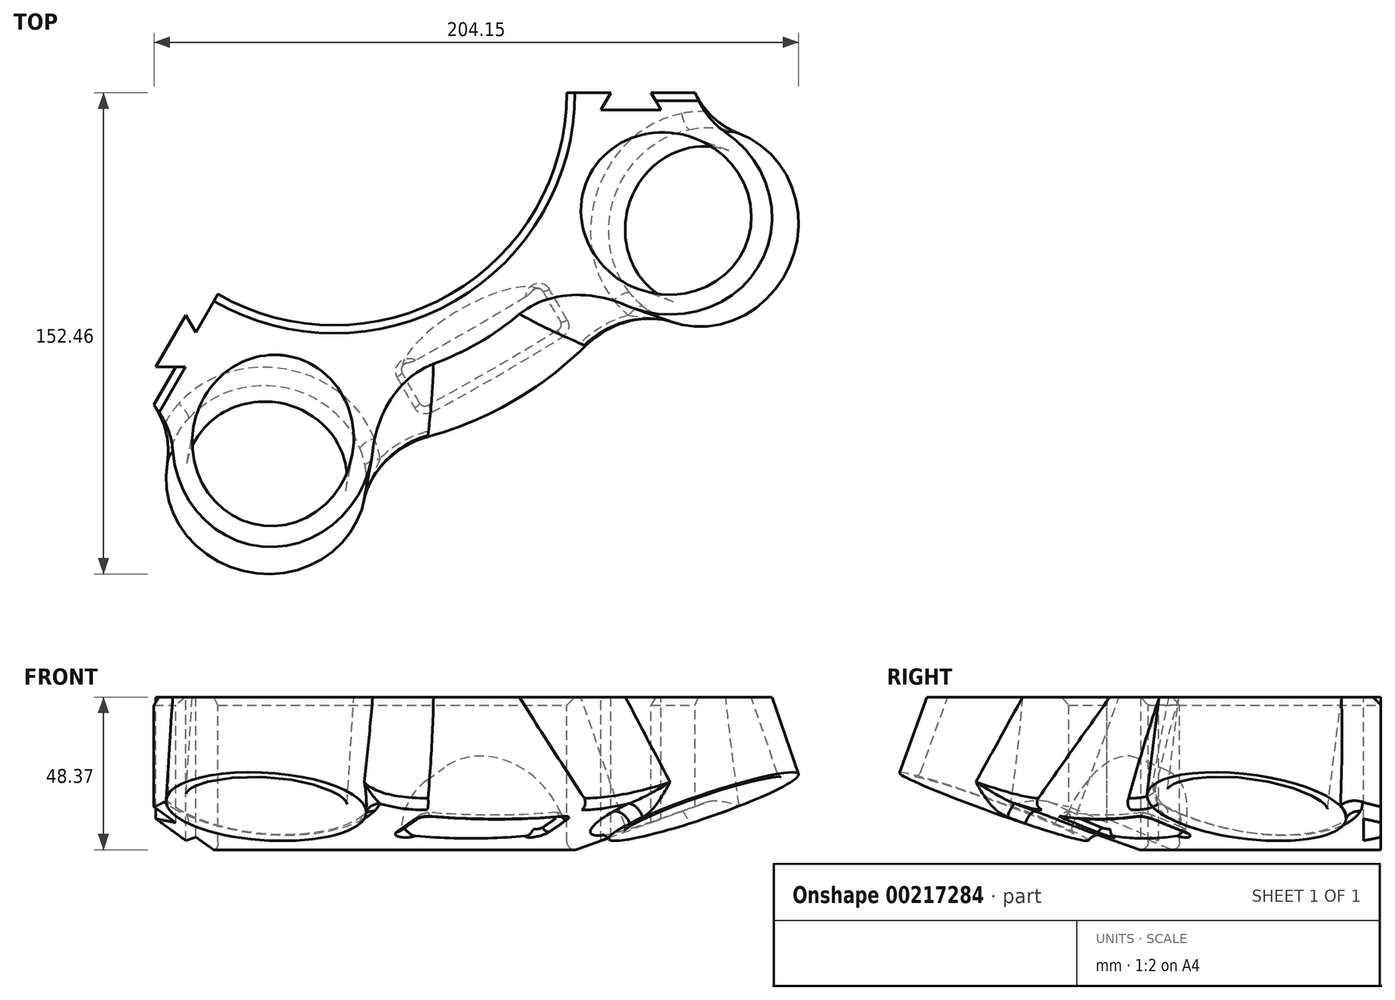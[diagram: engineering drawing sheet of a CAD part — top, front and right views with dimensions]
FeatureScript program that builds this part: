
annotation { "Feature Type Name" : "Feature", "Feature Type Description" : "" }
export const myFeature = defineFeature(function(context is Context, id is Id, definition is map)
    precondition{}
    {
        {
            var Q0;
            Q0=qCreatedBy(makeId("Top.planeOp"),FACE);
            var sketch = newSketch(context, id + "F0", { "sketchPlane" : qUnion([Q0])});
            skArc(sketch, "E0", {"start": v(36.2, 62.7) * mm, "mid": v(-36.2, 62.7) * mm, "end": v(-72.39, 0) * mm});
            skArc(sketch, "E1", {"start": v(55.44, 96.02) * mm, "mid": v(43.6, 101.94) * mm, "end": v(31.13, 106.41) * mm});
            skLineSegment(sketch, "E2", {"start": v(-72.4, 0) * mm, "end": v(-110.87, 0) * mm});
            skLineSegment(sketch, "E3", {"start": v(36.2, 62.7) * mm, "end": v(55.44, 96.02) * mm});
            skLineSegment(sketch, "E4", {"start": v(-22.63, 115.53) * mm, "end": v(0, 0) * mm, "construction": true});
            skLineSegment(sketch, "E5", {"start": v(-90.19, 75.67) * mm, "end": v(0, 0) * mm, "construction": true});
            skPoint(sketch, "E6.visualSharp", {"position": v(-104.04, 38.3) * mm});
            skPoint(sketch, "E7.visualSharp", {"position": v(-57.88, 98.1) * mm});
            skPoint(sketch, "E8.visualSharp", {"position": v(16.78, 109.6) * mm});
            skArc(sketch, "E9.converted", {"start": v(55.44, 96.02) * mm, "mid": v(-55.44, 96.02) * mm, "end": v(-110.87, 0) * mm});
            skSolve(sketch);
        }
        {
            var Q0;
            Q0=qCreatedBy(makeId("Front.planeOp"),FACE);
            var Q1;
            Q1=sQuery(id+"F0.wireOp",EDGE,"E5");
            cPlane(context, id + "F1", {"entities" : qUnion([Q0, Q1]), "cplaneType" : CPlaneType.LINE_ANGLE, "offset" : 25.4 * mm, "angle" : 0 * degree, "width" : 152.4 * mm, "height" : 152.4 * mm});
        }
        {
            var Q0;
            Q0=qCreatedBy(id+"F1.planeOp",FACE);
            var sketch = newSketch(context, id + "F2", { "sketchPlane" : qUnion([Q0])});
            skLineSegment(sketch, "E10", {"start": v(91.59, 0) * mm, "end": v(119.1, 10.02) * mm, "construction": true});
            skSolve(sketch);
        }
        {
            var Q0;
            Q0=qCreatedBy(id+"F1.planeOp",FACE);
            var Q1;
            Q1=sQuery(id+"F0.wireOp",EDGE,"E4");
            cPlane(context, id + "F3", {"entities" : qUnion([Q0, Q1]), "cplaneType" : CPlaneType.LINE_ANGLE, "offset" : 25.4 * mm, "angle" : 0 * degree, "width" : 152.4 * mm, "height" : 152.4 * mm});
        }
        {
            var Q0;
            Q0=qCreatedBy(id+"F3.planeOp",FACE);
            var sketch = newSketch(context, id + "F4", { "sketchPlane" : qUnion([Q0])});
            skLineSegment(sketch, "E11", {"start": v(-91.91, 0) * mm, "end": v(-139.27, 17.24) * mm, "construction": true});
            skSolve(sketch);
        }
        {
            var Q0;
            Q0=qCreatedBy(id+"F1.planeOp",FACE);
            var sketch = newSketch(context, id + "F5", { "sketchPlane" : qUnion([Q0])});
            skLineSegment(sketch, "E12", {"start": v(0, 0) * mm, "end": v(124.46, 0) * mm, "construction": true});
            skLineSegment(sketch, "E13", {"start": v(0, 53.66) * mm, "end": v(0, 0) * mm, "construction": true});
            skLineSegment(sketch, "E14", {"start": v(124.46, 0) * mm, "end": v(106, 50.72) * mm, "construction": true});
            skLineSegment(sketch, "E15", {"start": v(148.36, 8.7) * mm, "end": v(154.3, 10.86) * mm});
            skLineSegment(sketch, "E16", {"start": v(154.3, 10.86) * mm, "end": v(134.75, 64.56) * mm});
            skLineSegment(sketch, "E17", {"start": v(134.75, 64.56) * mm, "end": v(129.03, 61.8) * mm});
            skLineSegment(sketch, "E18", {"start": v(148.36, 8.7) * mm, "end": v(129.03, 61.8) * mm});
            skSolve(sketch);
        }
        {
            var Q0;
            Q0=qSketchRegion(id+"F5",true);
            var Q1;
            Q1=sQuery(id+"F5.wireOp",EDGE,"E14");
            revolve(context, id + "F6", {"entities" : qUnion([Q0]), "axis" : qUnion([Q1]), "revolveType" : RevolveType.FULL});
        }
        {
            var Q0;
            Q0=makeQuery(id+"F6.opRevolve","SWEPT_BODY",BODY,{"disambiguationData":[OSD([sQuery(id+"F5.wireOp",EDGE,"E15"),sQuery(id+"F5.wireOp",EDGE,"E16"),sQuery(id+"F5.wireOp",EDGE,"E17"),sQuery(id+"F5.wireOp",EDGE,"E18")])]});
            var Q1;
            Q1=sQuery(id+"F5.wireOp",EDGE,"E13");
            circularPattern(context, id + "F7", {"entities" : qUnion([Q0]), "axis" : qUnion([Q1]), "angle" : 40 * degree, "instanceCount" : 2});
        }
        {
            var Q0;
            Q0=qCreatedBy(id+"F1.planeOp",FACE);
            var sketch = newSketch(context, id + "F8", { "sketchPlane" : qUnion([Q0])});
            skLineSegment(sketch, "E19", {"start": v(73.66, 34.68) * mm, "end": v(73.66, -14.78) * mm});
            skLineSegment(sketch, "E20", {"start": v(73.66, -14.78) * mm, "end": v(73.66, 34.68) * mm});
            skLineSegment(sketch, "E21", {"start": v(73.66, 34.68) * mm, "end": v(91.44, 34.68) * mm});
            skLineSegment(sketch, "E22", {"start": v(114.27, 0) * mm, "end": v(73.66, -14.78) * mm});
            skLineSegment(sketch, "E23", {"start": v(91.44, 34.68) * mm, "end": v(114.27, 0) * mm});
            skSolve(sketch);
        }
        {
            var Q0;
            Q0=qSketchRegion(id+"F8",true);
            var Q1;
            Q1=sQuery(id+"F5.wireOp",EDGE,"E13");
            revolve(context, id + "F9", {"entities" : qUnion([Q0]), "axis" : qUnion([Q1]), "revolveType" : RevolveType.TWO_DIRECTIONS, "angle" : 80 * degree, "angleBack" : 320 * degree});
        }
        {
            var Q0;
            Q0=makeQuery(id+"F6.opRevolve","SWEPT_FACE",FACE,{"disambiguationData":[OSD([sQuery(id+"F5.wireOp",EDGE,"E15")])]});
            var sketch = newSketch(context, id + "F10", { "sketchPlane" : qUnion([Q0])});
            skCircle(sketch, "E24", {"center": v(-87.24, -77.9) * mm, "radius": 25.53 * mm});
            skSolve(sketch);
        }
        {
            var Q0;
            Q0=qSketchRegion(id+"F10",true);
            extrude(context, id + "F11", {"entities" : qUnion([Q0]), "operationType" : NewBodyOperationType.REMOVE, "endBound" : BoundingType.THROUGH_ALL, "depth" : 25.4 * mm, "hasSecondDirection" : true, "secondDirectionBound" : SecondDirectionBoundingType.THROUGH_ALL, "secondDirectionOppositeDirection" : true, "secondDirectionDepth" : 25.4 * mm});
        }
        {
            var Q0;
            Q0=makeQuery(id+"F7.opPattern","COPY",FACE,{"derivedFrom":makeQuery(id+"F6.opRevolve","SWEPT_FACE",FACE,{"disambiguationData":[OSD([sQuery(id+"F5.wireOp",EDGE,"E15")])]}),"instanceName":"1"});
            var sketch = newSketch(context, id + "F12", { "sketchPlane" : qUnion([Q0])});
            skCircle(sketch, "E25", {"center": v(-19.12, -115.38) * mm, "radius": 25.53 * mm});
            skSolve(sketch);
        }
        {
            var Q0;
            Q0=qSketchRegion(id+"F12",true);
            extrude(context, id + "F13", {"entities" : qUnion([Q0]), "operationType" : NewBodyOperationType.REMOVE, "endBound" : BoundingType.THROUGH_ALL, "depth" : 25.4 * mm, "hasSecondDirection" : true, "secondDirectionBound" : SecondDirectionBoundingType.THROUGH_ALL, "secondDirectionOppositeDirection" : true, "secondDirectionDepth" : 25.4 * mm});
        }
        {
            var Q0;
            Q0=makeQuery(id+"F9.opRevolve","CAP_FACE",FACE,{"disambiguationData":[OSD([sQuery(id+"F8.wireOp",EDGE,"E19"),sQuery(id+"F8.wireOp",EDGE,"E20"),sQuery(id+"F8.wireOp",EDGE,"E21"),sQuery(id+"F8.wireOp",EDGE,"E22"),sQuery(id+"F8.wireOp",EDGE,"E23")])],"isStart":true});
            var sketch = newSketch(context, id + "F14", { "sketchPlane" : qUnion([Q0])});
            skLineSegment(sketch, "E26", {"start": v(-73.66, 34.68) * mm, "end": v(-150.81, 34.68) * mm});
            skLineSegment(sketch, "E27", {"start": v(-150.81, 69.54) * mm, "end": v(-73.66, 69.54) * mm});
            skLineSegment(sketch, "E28", {"start": v(-150.81, 69.54) * mm, "end": v(-150.81, 34.68) * mm});
            skLineSegment(sketch, "E29", {"start": v(-73.66, 69.54) * mm, "end": v(-73.66, 34.68) * mm});
            skSolve(sketch);
        }
        {
            var Q0;
            Q0=qSketchRegion(id+"F14",true);
            var Q1;
            Q1=sQuery(id+"F5.wireOp",EDGE,"E13");
            revolve(context, id + "F15", {"operationType" : NewBodyOperationType.REMOVE, "entities" : qUnion([Q0]), "axis" : qUnion([Q1]), "revolveType" : RevolveType.ONE_DIRECTION, "angle" : 120 * degree});
        }
        {
            var Q0;
            Q0=makeQuery(id+"F6.opRevolve","SWEPT_BODY",BODY,{"disambiguationData":[OSD([sQuery(id+"F5.wireOp",EDGE,"E15"),sQuery(id+"F5.wireOp",EDGE,"E16"),sQuery(id+"F5.wireOp",EDGE,"E17"),sQuery(id+"F5.wireOp",EDGE,"E18")])]});
            var Q1;
            Q1=makeQuery(id+"F7.opPattern","COPY",BODY,{"derivedFrom":makeQuery(id+"F6.opRevolve","SWEPT_BODY",BODY,{"disambiguationData":[OSD([sQuery(id+"F5.wireOp",EDGE,"E15"),sQuery(id+"F5.wireOp",EDGE,"E16"),sQuery(id+"F5.wireOp",EDGE,"E17"),sQuery(id+"F5.wireOp",EDGE,"E18")])]}),"instanceName":"1"});
            var Q2;
            Q2=makeQuery(id+"F9.opRevolve","SWEPT_BODY",BODY,{"disambiguationData":[OSD([sQuery(id+"F8.wireOp",EDGE,"E19"),sQuery(id+"F8.wireOp",EDGE,"E20"),sQuery(id+"F8.wireOp",EDGE,"E21"),sQuery(id+"F8.wireOp",EDGE,"E22"),sQuery(id+"F8.wireOp",EDGE,"E23")])]});
            var Q3;
            Q3=sQuery(id+"F5.wireOp",EDGE,"E13");
            circularPattern(context, id + "F16", {"entities" : qUnion([Q0, Q1, Q2]), "axis" : qUnion([Q3]), "angle" : 120 * degree, "instanceCount" : 3});
        }
        {
            var Q0;
            Q0=qCreatedBy(makeId("Front.planeOp"),FACE);
            var sketch = newSketch(context, id + "F17", { "sketchPlane" : qUnion([Q0])});
            skLineSegment(sketch, "E30", {"start": v(-105.19, -47.93) * mm, "end": v(-151.02, -47.93) * mm, "construction": true});
            skLineSegment(sketch, "E31", {"start": v(-102.98, -8.48) * mm, "end": v(-100.37, -1.32) * mm});
            skLineSegment(sketch, "E32", {"start": v(-102.98, -8.48) * mm, "end": v(-129.23, 1.07) * mm});
            skLineSegment(sketch, "E33", {"start": v(-129.23, 1.07) * mm, "end": v(-126.63, 8.23) * mm});
            skLineSegment(sketch, "E34", {"start": v(-126.63, 8.23) * mm, "end": v(-100.37, -1.32) * mm});
            skLineSegment(sketch, "E35", {"start": v(-135.33, -8.25) * mm, "end": v(-127.68, 12.78) * mm, "construction": true});
            skSolve(sketch);
        }
        {
            var Q0;
            Q0=makeQuery(id+"FokKAQGzDr6NISq_2.opRevolve","SWEPT_BODY",BODY,{"disambiguationData":[OSD([sQuery(id+"F17.wireOp",EDGE,"E31"),sQuery(id+"F17.wireOp",EDGE,"E32"),sQuery(id+"F17.wireOp",EDGE,"E33"),sQuery(id+"F17.wireOp",EDGE,"E34")])]});
            var Q1;
            Q1=makeQuery(id+"F9.opRevolve","SWEPT_BODY",BODY,{"disambiguationData":[OSD([sQuery(id+"F8.wireOp",EDGE,"E19"),sQuery(id+"F8.wireOp",EDGE,"E20"),sQuery(id+"F8.wireOp",EDGE,"E21"),sQuery(id+"F8.wireOp",EDGE,"E22"),sQuery(id+"F8.wireOp",EDGE,"E23")])]});
            var Q2;
            Q2=sQuery(id+"F5.wireOp",EDGE,"E13");
            circularPattern(context, id + "F18", {"entities" : qUnion([Q0, Q1]), "axis" : qUnion([Q2]), "angle" : 120 * degree, "instanceCount" : 3});
        }
        {
            var Q0;
            {var subQ0=sQuery(id+"F8.wireOp",EDGE,"E22");var subQ2=sQuery(id+"F8.wireOp",EDGE,"E23");var subQ4=sQuery(id+"F8.wireOp",EDGE,"E21");var subQ5=makeQuery(id+"F11.opExtrude","SWEPT_FACE",FACE,{"disambiguationData":[OSD([sQuery(id+"F10.wireOp",EDGE,"E24")])]});Q0=makeQuery(id+"F16.opPattern","COPY",EDGE,{"derivedFrom":makeQuery(id+"F13.boolean.opBoolean","SPLIT",EDGE,{"disambiguationData":[TD([makeQuery(id+"F11.boolean.opBoolean","COPY",FACE,{"disambiguationData":[TD([makeQuery(id+"F9.opRevolve","SWEPT_FACE",FACE,{"disambiguationData":[OSD([subQ4])]})])],"derivedFrom":subQ5})])],"derivedFrom":makeQuery(id+"F11.boolean.opBoolean","SPLIT",EDGE,{"disambiguationData":[TD([makeQuery(id+"F9.opRevolve","CAP_FACE",FACE,{"disambiguationData":[OSD([sQuery(id+"F8.wireOp",EDGE,"E19"),sQuery(id+"F8.wireOp",EDGE,"E20"),subQ4,subQ0,subQ2])],"isStart":false})])],"derivedFrom":makeQuery(id+"F9.opRevolve","SWEPT_EDGE",EDGE,{"disambiguationData":[OSD([subQ0,subQ2])]})})}),"instanceName":"1"});}
            fillet(context, id + "F19", {"entities" : qUnion([Q0]), "radius" : 5.08 * mm, "tangentPropagation" : true, "allowEdgeOverflow" : false});
        }
        {
            var Q0;
            Q0=makeQuery(id+"F18.opPattern","COPY",BODY,{"derivedFrom":makeQuery(id+"FokKAQGzDr6NISq_2.opRevolve","SWEPT_BODY",BODY,{"disambiguationData":[OSD([sQuery(id+"F17.wireOp",EDGE,"E31"),sQuery(id+"F17.wireOp",EDGE,"E32"),sQuery(id+"F17.wireOp",EDGE,"E33"),sQuery(id+"F17.wireOp",EDGE,"E34")])]}),"instanceName":"1"});
            var Q1;
            Q1=makeQuery(id+"F6.opRevolve","SWEPT_BODY",BODY,{"disambiguationData":[OSD([sQuery(id+"F5.wireOp",EDGE,"E15"),sQuery(id+"F5.wireOp",EDGE,"E16"),sQuery(id+"F5.wireOp",EDGE,"E17"),sQuery(id+"F5.wireOp",EDGE,"E18")])]});
            var Q2;
            Q2=makeQuery(id+"F16.opPattern","COPY",BODY,{"derivedFrom":makeQuery(id+"F9.opRevolve","SWEPT_BODY",BODY,{"disambiguationData":[OSD([sQuery(id+"F8.wireOp",EDGE,"E19"),sQuery(id+"F8.wireOp",EDGE,"E20"),sQuery(id+"F8.wireOp",EDGE,"E21"),sQuery(id+"F8.wireOp",EDGE,"E22"),sQuery(id+"F8.wireOp",EDGE,"E23")])]}),"instanceName":"1"});
            var Q3;
            Q3=makeQuery(id+"F18.opPattern","COPY",BODY,{"derivedFrom":makeQuery(id+"F9.opRevolve","SWEPT_BODY",BODY,{"disambiguationData":[OSD([sQuery(id+"F8.wireOp",EDGE,"E19"),sQuery(id+"F8.wireOp",EDGE,"E20"),sQuery(id+"F8.wireOp",EDGE,"E21"),sQuery(id+"F8.wireOp",EDGE,"E22"),sQuery(id+"F8.wireOp",EDGE,"E23")])]}),"instanceName":"1"});
            var Q4;
            Q4=makeQuery(id+"F18.opPattern","COPY",BODY,{"derivedFrom":makeQuery(id+"F9.opRevolve","SWEPT_BODY",BODY,{"disambiguationData":[OSD([sQuery(id+"F8.wireOp",EDGE,"E19"),sQuery(id+"F8.wireOp",EDGE,"E20"),sQuery(id+"F8.wireOp",EDGE,"E21"),sQuery(id+"F8.wireOp",EDGE,"E22"),sQuery(id+"F8.wireOp",EDGE,"E23")])]}),"instanceName":"2"});
            var Q5;
            Q5=makeQuery(id+"F7.opPattern","COPY",BODY,{"derivedFrom":makeQuery(id+"F6.opRevolve","SWEPT_BODY",BODY,{"disambiguationData":[OSD([sQuery(id+"F5.wireOp",EDGE,"E15"),sQuery(id+"F5.wireOp",EDGE,"E16"),sQuery(id+"F5.wireOp",EDGE,"E17"),sQuery(id+"F5.wireOp",EDGE,"E18")])]}),"instanceName":"1"});
            var Q6;
            Q6=makeQuery(id+"F16.opPattern","COPY",BODY,{"derivedFrom":makeQuery(id+"F6.opRevolve","SWEPT_BODY",BODY,{"disambiguationData":[OSD([sQuery(id+"F5.wireOp",EDGE,"E15"),sQuery(id+"F5.wireOp",EDGE,"E16"),sQuery(id+"F5.wireOp",EDGE,"E17"),sQuery(id+"F5.wireOp",EDGE,"E18")])]}),"instanceName":"1"});
            var Q7;
            Q7=makeQuery(id+"FokKAQGzDr6NISq_2.opRevolve","SWEPT_BODY",BODY,{"disambiguationData":[OSD([sQuery(id+"F17.wireOp",EDGE,"E31"),sQuery(id+"F17.wireOp",EDGE,"E32"),sQuery(id+"F17.wireOp",EDGE,"E33"),sQuery(id+"F17.wireOp",EDGE,"E34")])]});
            var Q8;
            Q8=makeQuery(id+"F16.opPattern","COPY",BODY,{"derivedFrom":makeQuery(id+"F9.opRevolve","SWEPT_BODY",BODY,{"disambiguationData":[OSD([sQuery(id+"F8.wireOp",EDGE,"E19"),sQuery(id+"F8.wireOp",EDGE,"E20"),sQuery(id+"F8.wireOp",EDGE,"E21"),sQuery(id+"F8.wireOp",EDGE,"E22"),sQuery(id+"F8.wireOp",EDGE,"E23")])]}),"instanceName":"2"});
            var Q9;
            Q9=makeQuery(id+"F16.opPattern","COPY",BODY,{"derivedFrom":makeQuery(id+"F7.opPattern","COPY",BODY,{"derivedFrom":makeQuery(id+"F6.opRevolve","SWEPT_BODY",BODY,{"disambiguationData":[OSD([sQuery(id+"F5.wireOp",EDGE,"E15"),sQuery(id+"F5.wireOp",EDGE,"E16"),sQuery(id+"F5.wireOp",EDGE,"E17"),sQuery(id+"F5.wireOp",EDGE,"E18")])]}),"instanceName":"1"}),"instanceName":"2"});
            var Q10;
            Q10=makeQuery(id+"F18.opPattern","COPY",BODY,{"derivedFrom":makeQuery(id+"FokKAQGzDr6NISq_2.opRevolve","SWEPT_BODY",BODY,{"disambiguationData":[OSD([sQuery(id+"F17.wireOp",EDGE,"E31"),sQuery(id+"F17.wireOp",EDGE,"E32"),sQuery(id+"F17.wireOp",EDGE,"E33"),sQuery(id+"F17.wireOp",EDGE,"E34")])]}),"instanceName":"2"});
            var Q11;
            Q11=makeQuery(id+"F16.opPattern","COPY",BODY,{"derivedFrom":makeQuery(id+"F7.opPattern","COPY",BODY,{"derivedFrom":makeQuery(id+"F6.opRevolve","SWEPT_BODY",BODY,{"disambiguationData":[OSD([sQuery(id+"F5.wireOp",EDGE,"E15"),sQuery(id+"F5.wireOp",EDGE,"E16"),sQuery(id+"F5.wireOp",EDGE,"E17"),sQuery(id+"F5.wireOp",EDGE,"E18")])]}),"instanceName":"1"}),"instanceName":"1"});
            var Q12;
            Q12=makeQuery(id+"F16.opPattern","COPY",BODY,{"derivedFrom":makeQuery(id+"F6.opRevolve","SWEPT_BODY",BODY,{"disambiguationData":[OSD([sQuery(id+"F5.wireOp",EDGE,"E15"),sQuery(id+"F5.wireOp",EDGE,"E16"),sQuery(id+"F5.wireOp",EDGE,"E17"),sQuery(id+"F5.wireOp",EDGE,"E18")])]}),"instanceName":"2"});
            var Q13;
            Q13=makeQuery(id+"F9.opRevolve","SWEPT_BODY",BODY,{"disambiguationData":[OSD([sQuery(id+"F8.wireOp",EDGE,"E19"),sQuery(id+"F8.wireOp",EDGE,"E20"),sQuery(id+"F8.wireOp",EDGE,"E21"),sQuery(id+"F8.wireOp",EDGE,"E22"),sQuery(id+"F8.wireOp",EDGE,"E23")])]});
            booleanBodies(context, id + "F20", {"operationType" : BooleanOperationType.UNION, "tools" : qUnion([Q0, Q1, Q2, Q3, Q4, Q5, Q6, Q7, Q8, Q9, Q10, Q11, Q12, Q13])});
        }
        {
            var Q0;
            {var subQ0=sQuery(id+"F8.wireOp",EDGE,"E23");var subQ1=sQuery(id+"F8.wireOp",EDGE,"E22");var subQ2=sQuery(id+"F8.wireOp",EDGE,"E21");var subQ3=sQuery(id+"F8.wireOp",EDGE,"E20");var subQ4=sQuery(id+"F8.wireOp",EDGE,"E19");var subQ8=makeQuery(id+"F9.opRevolve","SWEPT_FACE",FACE,{"disambiguationData":[OSD([subQ0])]});var subQ9=makeQuery(id+"F11.boolean.opBoolean","SPLIT",FACE,{"disambiguationData":[TD([makeQuery(id+"F9.opRevolve","CAP_FACE",FACE,{"disambiguationData":[OSD([subQ4,subQ3,subQ2,subQ1,subQ0])],"isStart":true})])],"derivedFrom":subQ8});var subQ10=makeQuery(id+"F9.opRevolve","CAP_FACE",FACE,{"disambiguationData":[OSD([subQ4,subQ3,subQ2,subQ1,subQ0])],"isStart":false});Q0=makeQuery(id+"F20.opBoolean","INTERSECT",EDGE,{"derivedFrom":[makeQuery(id+"F13.boolean.opBoolean","SPLIT",FACE,{"disambiguationData":[TD([subQ10])],"derivedFrom":makeQuery(id+"F11.boolean.opBoolean","SPLIT",FACE,{"disambiguationData":[TD([subQ10])],"derivedFrom":subQ8})}),makeQuery(id+"F16.opPattern","COPY",FACE,{"derivedFrom":subQ9,"instanceName":"1"}),makeQuery(id+"F16.opPattern","COPY",FACE,{"derivedFrom":makeQuery(id+"F6.opRevolve","SWEPT_FACE",FACE,{"disambiguationData":[OSD([sQuery(id+"F5.wireOp",EDGE,"E16")])]}),"instanceName":"1"}),makeQuery(id+"F18.opPattern","COPY",FACE,{"derivedFrom":subQ9,"instanceName":"1"})]});}
            var Q1;
            {var subQ0=sQuery(id+"F8.wireOp",EDGE,"E23");var subQ1=sQuery(id+"F8.wireOp",EDGE,"E22");var subQ2=sQuery(id+"F8.wireOp",EDGE,"E21");Q1=makeQuery(id+"F20.opBoolean","INTERSECT",EDGE,{"derivedFrom":[makeQuery(id+"F11.boolean.opBoolean","SPLIT",FACE,{"disambiguationData":[TD([makeQuery(id+"F9.opRevolve","CAP_FACE",FACE,{"disambiguationData":[OSD([sQuery(id+"F8.wireOp",EDGE,"E19"),sQuery(id+"F8.wireOp",EDGE,"E20"),subQ2,subQ1,subQ0])],"isStart":true})])],"derivedFrom":makeQuery(id+"F9.opRevolve","SWEPT_FACE",FACE,{"disambiguationData":[OSD([subQ0])]})}),makeQuery(id+"F6.opRevolve","SWEPT_FACE",FACE,{"disambiguationData":[OSD([sQuery(id+"F5.wireOp",EDGE,"E16")])]})]});}
            var Q2;
            {var subQ0=sQuery(id+"F8.wireOp",EDGE,"E23");var subQ1=sQuery(id+"F8.wireOp",EDGE,"E22");var subQ2=sQuery(id+"F8.wireOp",EDGE,"E21");var subQ3=sQuery(id+"F8.wireOp",EDGE,"E20");var subQ4=sQuery(id+"F8.wireOp",EDGE,"E19");var subQ5=makeQuery(id+"F9.opRevolve","CAP_FACE",FACE,{"disambiguationData":[OSD([subQ4,subQ3,subQ2,subQ1,subQ0])],"isStart":false});var subQ9=makeQuery(id+"F9.opRevolve","SWEPT_FACE",FACE,{"disambiguationData":[OSD([subQ0])]});var subQ10=makeQuery(id+"F13.boolean.opBoolean","SPLIT",FACE,{"disambiguationData":[TD([subQ5])],"derivedFrom":makeQuery(id+"F11.boolean.opBoolean","SPLIT",FACE,{"disambiguationData":[TD([subQ5])],"derivedFrom":subQ9})});Q2=makeQuery(id+"F20.opBoolean","INTERSECT",EDGE,{"derivedFrom":[makeQuery(id+"F11.boolean.opBoolean","SPLIT",FACE,{"disambiguationData":[TD([makeQuery(id+"F9.opRevolve","CAP_FACE",FACE,{"disambiguationData":[OSD([subQ4,subQ3,subQ2,subQ1,subQ0])],"isStart":true})])],"derivedFrom":subQ9}),makeQuery(id+"F16.opPattern","COPY",FACE,{"derivedFrom":subQ10,"instanceName":"2"}),makeQuery(id+"F16.opPattern","COPY",FACE,{"derivedFrom":makeQuery(id+"F7.opPattern","COPY",FACE,{"derivedFrom":makeQuery(id+"F6.opRevolve","SWEPT_FACE",FACE,{"disambiguationData":[OSD([sQuery(id+"F5.wireOp",EDGE,"E16")])]}),"instanceName":"1"}),"instanceName":"2"}),makeQuery(id+"F18.opPattern","COPY",FACE,{"derivedFrom":subQ10,"instanceName":"2"})]});}
            var Q3;
            {var subQ0=sQuery(id+"F8.wireOp",EDGE,"E23");var subQ1=sQuery(id+"F8.wireOp",EDGE,"E22");var subQ2=sQuery(id+"F8.wireOp",EDGE,"E21");var subQ3=makeQuery(id+"F11.boolean.opBoolean","SPLIT",FACE,{"disambiguationData":[TD([makeQuery(id+"F9.opRevolve","CAP_FACE",FACE,{"disambiguationData":[OSD([sQuery(id+"F8.wireOp",EDGE,"E19"),sQuery(id+"F8.wireOp",EDGE,"E20"),subQ2,subQ1,subQ0])],"isStart":true})])],"derivedFrom":makeQuery(id+"F9.opRevolve","SWEPT_FACE",FACE,{"disambiguationData":[OSD([subQ0])]})});Q3=makeQuery(id+"F20.opBoolean","INTERSECT",EDGE,{"derivedFrom":[makeQuery(id+"F16.opPattern","COPY",FACE,{"derivedFrom":subQ3,"instanceName":"2"}),makeQuery(id+"F16.opPattern","COPY",FACE,{"derivedFrom":makeQuery(id+"F6.opRevolve","SWEPT_FACE",FACE,{"disambiguationData":[OSD([sQuery(id+"F5.wireOp",EDGE,"E16")])]}),"instanceName":"2"}),makeQuery(id+"F18.opPattern","COPY",FACE,{"derivedFrom":subQ3,"instanceName":"2"})]});}
            var Q4;
            {var subQ0=sQuery(id+"F8.wireOp",EDGE,"E23");var subQ1=sQuery(id+"F8.wireOp",EDGE,"E22");var subQ2=sQuery(id+"F8.wireOp",EDGE,"E21");var subQ3=sQuery(id+"F8.wireOp",EDGE,"E20");var subQ4=sQuery(id+"F8.wireOp",EDGE,"E19");var subQ8=makeQuery(id+"F9.opRevolve","SWEPT_FACE",FACE,{"disambiguationData":[OSD([subQ0])]});var subQ9=makeQuery(id+"F9.opRevolve","CAP_FACE",FACE,{"disambiguationData":[OSD([subQ4,subQ3,subQ2,subQ1,subQ0])],"isStart":false});var subQ10=makeQuery(id+"F13.boolean.opBoolean","SPLIT",FACE,{"disambiguationData":[TD([subQ9])],"derivedFrom":makeQuery(id+"F11.boolean.opBoolean","SPLIT",FACE,{"disambiguationData":[TD([subQ9])],"derivedFrom":subQ8})});Q4=makeQuery(id+"F20.opBoolean","INTERSECT",EDGE,{"derivedFrom":[makeQuery(id+"F16.opPattern","COPY",FACE,{"derivedFrom":subQ10,"instanceName":"1"}),makeQuery(id+"F16.opPattern","COPY",FACE,{"derivedFrom":makeQuery(id+"F7.opPattern","COPY",FACE,{"derivedFrom":makeQuery(id+"F6.opRevolve","SWEPT_FACE",FACE,{"disambiguationData":[OSD([sQuery(id+"F5.wireOp",EDGE,"E16")])]}),"instanceName":"1"}),"instanceName":"1"}),makeQuery(id+"F18.opPattern","COPY",FACE,{"derivedFrom":subQ10,"instanceName":"1"}),makeQuery(id+"F18.opPattern","COPY",FACE,{"derivedFrom":makeQuery(id+"F11.boolean.opBoolean","SPLIT",FACE,{"disambiguationData":[TD([makeQuery(id+"F9.opRevolve","CAP_FACE",FACE,{"disambiguationData":[OSD([subQ4,subQ3,subQ2,subQ1,subQ0])],"isStart":true})])],"derivedFrom":subQ8}),"instanceName":"2"})]});}
            var Q5;
            {var subQ0=sQuery(id+"F8.wireOp",EDGE,"E23");var subQ1=sQuery(id+"F8.wireOp",EDGE,"E22");var subQ2=sQuery(id+"F8.wireOp",EDGE,"E21");var subQ3=makeQuery(id+"F9.opRevolve","CAP_FACE",FACE,{"disambiguationData":[OSD([sQuery(id+"F8.wireOp",EDGE,"E19"),sQuery(id+"F8.wireOp",EDGE,"E20"),subQ2,subQ1,subQ0])],"isStart":false});Q5=makeQuery(id+"F20.opBoolean","INTERSECT",EDGE,{"derivedFrom":[makeQuery(id+"F13.boolean.opBoolean","SPLIT",FACE,{"disambiguationData":[TD([subQ3])],"derivedFrom":makeQuery(id+"F11.boolean.opBoolean","SPLIT",FACE,{"disambiguationData":[TD([subQ3])],"derivedFrom":makeQuery(id+"F9.opRevolve","SWEPT_FACE",FACE,{"disambiguationData":[OSD([subQ0])]})})}),makeQuery(id+"F7.opPattern","COPY",FACE,{"derivedFrom":makeQuery(id+"F6.opRevolve","SWEPT_FACE",FACE,{"disambiguationData":[OSD([sQuery(id+"F5.wireOp",EDGE,"E16")])]}),"instanceName":"1"})]});}
            fillet(context, id + "F21", {"entities" : qUnion([Q0, Q1, Q2, Q3, Q4, Q5]), "radius" : 25.4 * mm, "tangentPropagation" : true, "allowEdgeOverflow" : false});
        }
        {
            var Q0;
            Q0=qCreatedBy(makeId("Right.planeOp"),FACE);
            var Q1;
            Q1=sQuery(id+"F17.wireOp",EDGE,"E31");
            cPlane(context, id + "F22", {"entities" : qUnion([Q0, Q1]), "cplaneType" : CPlaneType.LINE_ANGLE, "offset" : 25.4 * mm, "angle" : 0 * degree, "width" : 152.4 * mm, "height" : 152.4 * mm});
        }
        {
            var Q0;
            Q0=qCreatedBy(id+"F22.planeOp",FACE);
            var sketch = newSketch(context, id + "F23", { "sketchPlane" : qUnion([Q0])});
            skCircle(sketch, "E36", {"center": v(0, -43.2) * mm, "radius": 26.67 * mm});
            skSolve(sketch);
        }
        {
            var Q0;
            Q0=qSketchRegion(id+"F23",true);
            extrude(context, id + "F24", {"entities" : qUnion([Q0]), "oppositeDirection" : true, "depth" : 16 * mm});
        }
        {
            var Q0;
            Q0=makeQuery(id+"F24.opExtrude","SWEPT_BODY",BODY,{"disambiguationData":[OSD([sQuery(id+"F23.wireOp",EDGE,"E36")])]});
            var Q1;
            Q1=sQuery(id+"F5.wireOp",EDGE,"E13");
            circularPattern(context, id + "F25", {"operationType" : NewBodyOperationType.REMOVE, "entities" : qUnion([Q0]), "axis" : qUnion([Q1]), "angle" : 120 * degree, "instanceCount" : 3});
        }
        {
            var Q0;
            Q0=qCreatedBy(makeId("Top.planeOp"),FACE);
            var sketch = newSketch(context, id + "F26", { "sketchPlane" : qUnion([Q0])});
            skLineSegment(sketch, "E37", {"start": v(0, 0) * mm, "end": v(193.48, 0) * mm});
            skLineSegment(sketch, "E38", {"start": v(0, 0) * mm, "end": v(-96.74, -167.56) * mm});
            skArc(sketch, "E39", {"start": v(193.48, 0) * mm, "mid": v(-96.74, 167.56) * mm, "end": v(-96.74, -167.56) * mm});
            skSolve(sketch);
        }
        {
            var Q0;
            Q0=qSketchRegion(id+"F26",true);
            extrude(context, id + "F27", {"entities" : qUnion([Q0]), "operationType" : NewBodyOperationType.REMOVE, "endBound" : BoundingType.THROUGH_ALL, "oppositeDirection" : true, "depth" : 25.4 * mm, "hasSecondDirection" : true, "secondDirectionBound" : SecondDirectionBoundingType.THROUGH_ALL, "secondDirectionOppositeDirection" : false, "secondDirectionDepth" : 25.4 * mm});
        }
        {
            var Q0;
            {var subQ0=makeQuery(id+"F9.opRevolve","SWEPT_FACE",FACE,{"disambiguationData":[OSD([sQuery(id+"F8.wireOp",EDGE,"E21")])]});var subQ1=makeQuery(id+"F6.opRevolve","SWEPT_FACE",FACE,{"disambiguationData":[OSD([sQuery(id+"F5.wireOp",EDGE,"E16")])]});var subQ4=makeQuery(id+"F15.opRevolve","SWEPT_FACE",FACE,{"disambiguationData":[OSD([sQuery(id+"F14.wireOp",EDGE,"E26")])]});var subQ5=makeQuery(id+"F15.boolean.opBoolean","COPY",FACE,{"disambiguationData":[TD([makeQuery(id+"F7.opPattern","COPY",FACE,{"derivedFrom":subQ1,"instanceName":"1"})])],"derivedFrom":subQ4});var subQ6=makeQuery(id+"F15.boolean.opBoolean","COPY",FACE,{"disambiguationData":[TD([subQ1])],"derivedFrom":subQ4});Q0=makeQuery(id+"F34.boolean.opBoolean","MERGE",FACE,{"derivedFrom":[makeQuery(id+"F20.opBoolean","MERGE",FACE,{"derivedFrom":[subQ0,subQ6,subQ5,makeQuery(id+"F16.opPattern","COPY",FACE,{"derivedFrom":subQ0,"instanceName":"1"}),makeQuery(id+"F16.opPattern","COPY",FACE,{"derivedFrom":subQ6,"instanceName":"1"}),makeQuery(id+"F16.opPattern","COPY",FACE,{"derivedFrom":subQ5,"instanceName":"1"}),makeQuery(id+"F16.opPattern","COPY",FACE,{"derivedFrom":subQ0,"instanceName":"2"}),makeQuery(id+"F16.opPattern","COPY",FACE,{"derivedFrom":subQ6,"instanceName":"2"}),makeQuery(id+"F16.opPattern","COPY",FACE,{"derivedFrom":subQ5,"instanceName":"2"}),makeQuery(id+"F18.opPattern","COPY",FACE,{"derivedFrom":subQ0,"instanceName":"1"}),makeQuery(id+"F18.opPattern","COPY",FACE,{"derivedFrom":subQ0,"instanceName":"2"})]}),makeQuery(id+"F34.opExtrude","CAP_FACE",FACE,{"disambiguationData":[OSD([sQuery(id+"F33.wireOp",EDGE,"E51"),sQuery(id+"F33.wireOp",EDGE,"E52"),sQuery(id+"F33.wireOp",EDGE,"E53"),sQuery(id+"F33.wireOp",EDGE,"E54")])],"isStart":true})]});}
            var sketch = newSketch(context, id + "F28", { "sketchPlane" : qUnion([Q0])});
            skLineSegment(sketch, "E40", {"start": v(87.63, 0) * mm, "end": v(100.33, 0) * mm});
            skLineSegment(sketch, "E41", {"start": v(73.66, 0) * mm, "end": v(73.66, -14.95) * mm, "construction": true});
            skLineSegment(sketch, "E42", {"start": v(87.63, 0) * mm, "end": v(84.45, -5.5) * mm});
            skLineSegment(sketch, "E43", {"start": v(84.45, -5.5) * mm, "end": v(103.5, -5.5) * mm});
            skLineSegment(sketch, "E44", {"start": v(103.5, -5.5) * mm, "end": v(100.33, 0) * mm});
            skSolve(sketch);
        }
        {
            var Q0;
            {var subQ12=sQuery(id+"F33.wireOp",EDGE,"E53");Q0=makeQuery(id+"F34.boolean.opBoolean","SPLIT",FACE,{"disambiguationData":[TD([makeQuery(id+"F34.opExtrude","SWEPT_FACE",FACE,{"disambiguationData":[OSD([subQ12])]})])],"derivedFrom":makeQuery(id+"F27.boolean.opBoolean","COPY",FACE,{"derivedFrom":makeQuery(id+"F27.opExtrude","SWEPT_FACE",FACE,{"disambiguationData":[OSD([sQuery(id+"F26.wireOp",EDGE,"E38")])]})})});}
            var sketch = newSketch(context, id + "F29", { "sketchPlane" : qUnion([Q0])});
            skLineSegment(sketch, "E45", {"start": v(114.27, 0) * mm, "end": v(91.44, 34.68) * mm});
            skLineSegment(sketch, "E46", {"start": v(91.44, 34.68) * mm, "end": v(114.27, 34.68) * mm});
            skLineSegment(sketch, "E47", {"start": v(114.27, 34.68) * mm, "end": v(114.27, 0) * mm});
            skSolve(sketch);
        }
        {
            var Q0;
            Q0=makeQuery(id+"F29.imprint","IMPRINT",FACE,{"disambiguationData":[TD([[makeQuery(id+"F29.imprint","IMPRINT",EDGE,{"derivedFrom":sQuery(id+"F29.wireOp",EDGE,"E45")}),1.0]])]});
            var Q1;
            Q1=qConstructionFilter(qBodyType(qCreatedBy(id+"F29",EDGE),BodyType.WIRE),ConstructionObject.NO);
            var Q2;
            Q2=sQuery(id+"F5.wireOp",EDGE,"E13");
            revolve(context, id + "F30", {"operationType" : NewBodyOperationType.ADD, "entities" : qUnion([Q0]), "surfaceEntities" : qUnion([Q1]), "axis" : qUnion([Q2]), "revolveType" : RevolveType.ONE_DIRECTION, "oppositeDirection" : true, "angle" : 6 * degree});
        }
        {
            var Q0;
            Q0=makeQuery(id+"F35.boolean.opBoolean","SPLIT",FACE,{"disambiguationData":[TD([makeQuery(id+"F35.opExtrude","SWEPT_FACE",FACE,{"disambiguationData":[OSD([sQuery(id+"F28.wireOp",EDGE,"E44")])]})])],"derivedFrom":makeQuery(id+"F27.boolean.opBoolean","COPY",FACE,{"derivedFrom":makeQuery(id+"F27.opExtrude","SWEPT_FACE",FACE,{"disambiguationData":[OSD([sQuery(id+"F26.wireOp",EDGE,"E37")])]})})});
            var sketch = newSketch(context, id + "F31", { "sketchPlane" : qUnion([Q0])});
            skLineSegment(sketch, "E48", {"start": v(-114.27, 0) * mm, "end": v(-114.27, 34.68) * mm});
            skLineSegment(sketch, "E49", {"start": v(-114.27, 34.68) * mm, "end": v(-91.44, 34.68) * mm});
            skLineSegment(sketch, "E50", {"start": v(-91.44, 34.68) * mm, "end": v(-114.27, 0) * mm});
            skSolve(sketch);
        }
        {
            var Q0;
            Q0=qSketchRegion(id+"F31",true);
            var Q1;
            Q1=sQuery(id+"F5.wireOp",EDGE,"E13");
            revolve(context, id + "F32", {"operationType" : NewBodyOperationType.ADD, "entities" : qUnion([Q0]), "axis" : qUnion([Q1]), "revolveType" : RevolveType.ONE_DIRECTION, "angle" : 6 * degree});
        }
        {
            var Q0;
            {var subQ0=makeQuery(id+"F9.opRevolve","SWEPT_FACE",FACE,{"disambiguationData":[OSD([sQuery(id+"F8.wireOp",EDGE,"E21")])]});var subQ1=makeQuery(id+"F6.opRevolve","SWEPT_FACE",FACE,{"disambiguationData":[OSD([sQuery(id+"F5.wireOp",EDGE,"E16")])]});var subQ4=makeQuery(id+"F15.opRevolve","SWEPT_FACE",FACE,{"disambiguationData":[OSD([sQuery(id+"F14.wireOp",EDGE,"E26")])]});var subQ5=makeQuery(id+"F15.boolean.opBoolean","COPY",FACE,{"disambiguationData":[TD([makeQuery(id+"F7.opPattern","COPY",FACE,{"derivedFrom":subQ1,"instanceName":"1"})])],"derivedFrom":subQ4});var subQ6=makeQuery(id+"F15.boolean.opBoolean","COPY",FACE,{"disambiguationData":[TD([subQ1])],"derivedFrom":subQ4});Q0=makeQuery(id+"F20.opBoolean","MERGE",FACE,{"derivedFrom":[subQ0,subQ6,subQ5,makeQuery(id+"F16.opPattern","COPY",FACE,{"derivedFrom":subQ0,"instanceName":"1"}),makeQuery(id+"F16.opPattern","COPY",FACE,{"derivedFrom":subQ6,"instanceName":"1"}),makeQuery(id+"F16.opPattern","COPY",FACE,{"derivedFrom":subQ5,"instanceName":"1"}),makeQuery(id+"F16.opPattern","COPY",FACE,{"derivedFrom":subQ0,"instanceName":"2"}),makeQuery(id+"F16.opPattern","COPY",FACE,{"derivedFrom":subQ6,"instanceName":"2"}),makeQuery(id+"F16.opPattern","COPY",FACE,{"derivedFrom":subQ5,"instanceName":"2"}),makeQuery(id+"F18.opPattern","COPY",FACE,{"derivedFrom":subQ0,"instanceName":"1"}),makeQuery(id+"F18.opPattern","COPY",FACE,{"derivedFrom":subQ0,"instanceName":"2"})]});}
            var sketch = newSketch(context, id + "F33", { "sketchPlane" : qUnion([Q0])});
            skLineSegment(sketch, "E51", {"start": v(-43.84, -75.93) * mm, "end": v(-47.02, -70.43) * mm});
            skLineSegment(sketch, "E52", {"start": v(-47.02, -70.43) * mm, "end": v(-56.49, -86.84) * mm});
            skLineSegment(sketch, "E53", {"start": v(-56.49, -86.84) * mm, "end": v(-50.14, -86.84) * mm});
            skLineSegment(sketch, "E54", {"start": v(-50.14, -86.84) * mm, "end": v(-43.84, -75.93) * mm});
            skLineSegment(sketch, "E55", {"start": v(-57.13, -98.96) * mm, "end": v(-64.69, -94.6) * mm, "construction": true});
            skSolve(sketch);
        }
        {
            var Q0;
            Q0=qSketchRegion(id+"F33",true);
            var Q1;
            {var subQ0=makeQuery(id+"F9.opRevolve","SWEPT_FACE",FACE,{"disambiguationData":[OSD([sQuery(id+"F8.wireOp",EDGE,"E22")])]});Q1=makeQuery(id+"F20.opBoolean","MERGE",FACE,{"derivedFrom":[subQ0,makeQuery(id+"F16.opPattern","COPY",FACE,{"derivedFrom":subQ0,"instanceName":"2"}),makeQuery(id+"F18.opPattern","COPY",FACE,{"derivedFrom":subQ0,"instanceName":"1"}),makeQuery(id+"F18.opPattern","COPY",FACE,{"derivedFrom":subQ0,"instanceName":"2"}),makeQuery(id+"F16.opPattern","COPY",FACE,{"derivedFrom":subQ0,"instanceName":"1"})]});}
            extrude(context, id + "F34", {"entities" : qUnion([Q0]), "operationType" : NewBodyOperationType.ADD, "endBound" : BoundingType.UP_TO_SURFACE, "oppositeDirection" : true, "endBoundEntityFace" : qUnion([Q1]), "depth" : 25.4 * mm});
        }
        {
            var Q0;
            Q0=qSketchRegion(id+"F28",true);
            var Q1;
            {var subQ0=sQuery(id+"F8.wireOp",EDGE,"E22");var subQ1=makeQuery(id+"F9.opRevolve","SWEPT_FACE",FACE,{"disambiguationData":[OSD([subQ0])]});Q1=makeQuery(id+"F34.boolean.opBoolean","MERGE",FACE,{"derivedFrom":[makeQuery(id+"F20.opBoolean","MERGE",FACE,{"derivedFrom":[subQ1,makeQuery(id+"F16.opPattern","COPY",FACE,{"derivedFrom":subQ1,"instanceName":"2"}),makeQuery(id+"F18.opPattern","COPY",FACE,{"derivedFrom":subQ1,"instanceName":"1"}),makeQuery(id+"F18.opPattern","COPY",FACE,{"derivedFrom":subQ1,"instanceName":"2"}),makeQuery(id+"F16.opPattern","COPY",FACE,{"derivedFrom":subQ1,"instanceName":"1"})]}),makeQuery(id+"F34.opExtrude","CAP_FACE",FACE,{"disambiguationData":[OSD([subQ0])],"isStart":false})]});}
            extrude(context, id + "F35", {"entities" : qUnion([Q0]), "operationType" : NewBodyOperationType.REMOVE, "endBound" : BoundingType.UP_TO_SURFACE, "oppositeDirection" : true, "endBoundEntityFace" : qUnion([Q1]), "depth" : 25.4 * mm});
        }
        {
            var Q0;
            Q0=makeQuery(id+"F30.boolean.opBoolean","INTERSECT",EDGE,{"derivedFrom":[makeQuery(id+"F16.opPattern","COPY",FACE,{"derivedFrom":makeQuery(id+"F6.opRevolve","SWEPT_FACE",FACE,{"disambiguationData":[OSD([sQuery(id+"F5.wireOp",EDGE,"E16")])]}),"instanceName":"2"}),makeQuery(id+"F30.opRevolve","SWEPT_FACE",FACE,{"disambiguationData":[OSD([sQuery(id+"F29.wireOp",EDGE,"E47")])]})]});
            var Q1;
            Q1=makeQuery(id+"F32.boolean.opBoolean","INTERSECT",EDGE,{"derivedFrom":[makeQuery(id+"F16.opPattern","COPY",FACE,{"derivedFrom":makeQuery(id+"F7.opPattern","COPY",FACE,{"derivedFrom":makeQuery(id+"F6.opRevolve","SWEPT_FACE",FACE,{"disambiguationData":[OSD([sQuery(id+"F5.wireOp",EDGE,"E16")])]}),"instanceName":"1"}),"instanceName":"1"}),makeQuery(id+"F32.opRevolve","SWEPT_FACE",FACE,{"disambiguationData":[OSD([sQuery(id+"F31.wireOp",EDGE,"E48")])]})]});
            fillet(context, id + "F36", {"entities" : qUnion([Q0, Q1]), "radius" : 25.4 * mm, "tangentPropagation" : true, "allowEdgeOverflow" : false});
        }
        {
            var Q0;
            {var subQ0=makeQuery(id+"F9.opRevolve","SWEPT_EDGE",EDGE,{"disambiguationData":[OSD([sQuery(id+"F8.wireOp",EDGE,"E20"),sQuery(id+"F8.wireOp",EDGE,"E21")])]});Q0=makeQuery(id+"F20.opBoolean","MERGE",EDGE,{"derivedFrom":[subQ0,makeQuery(id+"F16.opPattern","COPY",EDGE,{"derivedFrom":subQ0,"instanceName":"1"}),makeQuery(id+"F16.opPattern","COPY",EDGE,{"derivedFrom":subQ0,"instanceName":"2"}),makeQuery(id+"F18.opPattern","COPY",EDGE,{"derivedFrom":subQ0,"instanceName":"1"}),makeQuery(id+"F18.opPattern","COPY",EDGE,{"derivedFrom":subQ0,"instanceName":"2"})]});}
            chamfer(context, id + "F37", {"entities" : qUnion([Q0]), "width" : 2.54 * mm, "tangentPropagation" : true});
        }
        {
            var Q0;
            Q0=makeQuery(id+"F16.opPattern","COPY",EDGE,{"derivedFrom":makeQuery(id+"F11.boolean.opBoolean","INTERSECT",EDGE,{"derivedFrom":[makeQuery(id+"F6.opRevolve","SWEPT_FACE",FACE,{"disambiguationData":[OSD([sQuery(id+"F5.wireOp",EDGE,"E15")])]}),makeQuery(id+"F11.opExtrude","SWEPT_FACE",FACE,{"disambiguationData":[OSD([sQuery(id+"F10.wireOp",EDGE,"E24")])]})]}),"instanceName":"2"});
            var Q1;
            Q1=makeQuery(id+"F16.opPattern","COPY",EDGE,{"derivedFrom":makeQuery(id+"F13.boolean.opBoolean","INTERSECT",EDGE,{"derivedFrom":[makeQuery(id+"F7.opPattern","COPY",FACE,{"derivedFrom":makeQuery(id+"F6.opRevolve","SWEPT_FACE",FACE,{"disambiguationData":[OSD([sQuery(id+"F5.wireOp",EDGE,"E15")])]}),"instanceName":"1"}),makeQuery(id+"F13.opExtrude","SWEPT_FACE",FACE,{"disambiguationData":[OSD([sQuery(id+"F12.wireOp",EDGE,"E25")])]})]}),"instanceName":"1"});
            fillet(context, id + "F38", {"entities" : qUnion([Q0, Q1]), "radius" : 2.54 * mm, "tangentPropagation" : true, "allowEdgeOverflow" : false});
        }
        {
            var Q0;
            {var subQ0=sQuery(id+"F8.wireOp",EDGE,"E23");var subQ1=sQuery(id+"F8.wireOp",EDGE,"E22");var subQ2=sQuery(id+"F8.wireOp",EDGE,"E21");var subQ3=sQuery(id+"F8.wireOp",EDGE,"E20");var subQ7=makeQuery(id+"F9.opRevolve","SWEPT_EDGE",EDGE,{"disambiguationData":[OSD([subQ1,subQ0])]});var subQ8=makeQuery(id+"F9.opRevolve","CAP_FACE",FACE,{"disambiguationData":[OSD([subQ3,subQ2,subQ1,subQ0])],"isStart":false});var subQ9=makeQuery(id+"F13.boolean.opBoolean","SPLIT",EDGE,{"disambiguationData":[TD([subQ8])],"derivedFrom":makeQuery(id+"F11.boolean.opBoolean","SPLIT",EDGE,{"disambiguationData":[TD([subQ8])],"derivedFrom":subQ7})});Q0=makeQuery(id+"F20.opBoolean","MERGE",EDGE,{"derivedFrom":[makeQuery(id+"F16.opPattern","COPY",EDGE,{"derivedFrom":subQ9,"instanceName":"1"}),makeQuery(id+"F18.opPattern","COPY",EDGE,{"derivedFrom":subQ9,"instanceName":"1"}),makeQuery(id+"F18.opPattern","COPY",EDGE,{"derivedFrom":makeQuery(id+"F11.boolean.opBoolean","SPLIT",EDGE,{"disambiguationData":[TD([makeQuery(id+"F9.opRevolve","CAP_FACE",FACE,{"disambiguationData":[OSD([subQ3,subQ2,subQ1,subQ0])],"isStart":true})])],"derivedFrom":subQ7}),"instanceName":"2"})]});}
            var Q1;
            {var subQ0=makeQuery(id+"F9.opRevolve","SWEPT_EDGE",EDGE,{"disambiguationData":[OSD([sQuery(id+"F8.wireOp",EDGE,"E20"),sQuery(id+"F8.wireOp",EDGE,"E22")])]});Q1=makeQuery(id+"F20.opBoolean","MERGE",EDGE,{"derivedFrom":[subQ0,makeQuery(id+"F16.opPattern","COPY",EDGE,{"derivedFrom":subQ0,"instanceName":"1"}),makeQuery(id+"F16.opPattern","COPY",EDGE,{"derivedFrom":subQ0,"instanceName":"2"}),makeQuery(id+"F18.opPattern","COPY",EDGE,{"derivedFrom":subQ0,"instanceName":"1"}),makeQuery(id+"F18.opPattern","COPY",EDGE,{"derivedFrom":subQ0,"instanceName":"2"})]});}
            fillet(context, id + "F39", {"entities" : qUnion([Q0, Q1]), "radius" : 2.54 * mm, "tangentPropagation" : true, "allowEdgeOverflow" : false});
        }
        {
            var Q0;
            {var subQ0=makeQuery(id+"F9.opRevolve","SWEPT_FACE",FACE,{"disambiguationData":[OSD([sQuery(id+"F8.wireOp",EDGE,"E21")])]});var subQ1=subQ0;var subQ2=makeQuery(id+"F16.opPattern","COPY",FACE,{"derivedFrom":subQ1,"instanceName":"2"});var subQ3=makeQuery(id+"F6.opRevolve","SWEPT_FACE",FACE,{"disambiguationData":[OSD([sQuery(id+"F5.wireOp",EDGE,"E16")])]});var subQ6=makeQuery(id+"F15.opRevolve","SWEPT_FACE",FACE,{"disambiguationData":[OSD([sQuery(id+"F14.wireOp",EDGE,"E26")])]});var subQ7=makeQuery(id+"F15.boolean.opBoolean","COPY",FACE,{"disambiguationData":[TD([subQ3])],"derivedFrom":subQ6});var subQ8=makeQuery(id+"F16.opPattern","COPY",FACE,{"derivedFrom":subQ7,"instanceName":"1"});var subQ9=makeQuery(id+"F15.boolean.opBoolean","COPY",FACE,{"disambiguationData":[TD([makeQuery(id+"F7.opPattern","COPY",FACE,{"derivedFrom":subQ3,"instanceName":"1"})])],"derivedFrom":subQ6});var subQ10=makeQuery(id+"F16.opPattern","COPY",FACE,{"derivedFrom":subQ9,"instanceName":"1"});var subQ12=makeQuery(id+"F16.opPattern","COPY",FACE,{"derivedFrom":subQ1,"instanceName":"1"});var subQ13=makeQuery(id+"F9.opRevolve","SWEPT_FACE",FACE,{"disambiguationData":[OSD([sQuery(id+"F8.wireOp",EDGE,"E20")])]});var subQ14=makeQuery(id+"F16.opPattern","COPY",FACE,{"derivedFrom":subQ7,"instanceName":"2"});var subQ15=makeQuery(id+"F16.opPattern","COPY",FACE,{"derivedFrom":subQ9,"instanceName":"2"});var subQ16=makeQuery(id+"F18.opPattern","COPY",FACE,{"derivedFrom":subQ1,"instanceName":"1"});var subQ17=makeQuery(id+"F18.opPattern","COPY",FACE,{"derivedFrom":subQ1,"instanceName":"2"});var subQ18=sQuery(id+"F29.wireOp",EDGE,"E46");var subQ19=makeQuery(id+"F27.opExtrude","SWEPT_FACE",FACE,{"disambiguationData":[OSD([sQuery(id+"F26.wireOp",EDGE,"E38")])]});Q0=makeQuery(id+"F34.boolean.opBoolean","SPLIT",EDGE,{"disambiguationData":[TD([subQ13])],"derivedFrom":makeQuery(id+"F30.boolean.opBoolean","MERGE",EDGE,{"derivedFrom":[makeQuery(id+"F27.boolean.opBoolean","INTERSECT",EDGE,{"derivedFrom":[makeQuery(id+"F20.opBoolean","MERGE",FACE,{"derivedFrom":[subQ1,subQ7,subQ9,subQ12,subQ8,subQ10,subQ2,subQ14,subQ15,subQ16,subQ17]}),subQ19]}),makeQuery(id+"F30.opRevolve","CAP_EDGE",EDGE,{"disambiguationData":[OSD([subQ18])],"isStart":true})]})});}
            var Q1;
            {var subQ0=makeQuery(id+"F6.opRevolve","SWEPT_FACE",FACE,{"disambiguationData":[OSD([sQuery(id+"F5.wireOp",EDGE,"E16")])]});var subQ3=makeQuery(id+"F15.opRevolve","SWEPT_FACE",FACE,{"disambiguationData":[OSD([sQuery(id+"F14.wireOp",EDGE,"E26")])]});var subQ4=makeQuery(id+"F15.boolean.opBoolean","COPY",FACE,{"disambiguationData":[TD([makeQuery(id+"F7.opPattern","COPY",FACE,{"derivedFrom":subQ0,"instanceName":"1"})])],"derivedFrom":subQ3});var subQ5=makeQuery(id+"F16.opPattern","COPY",FACE,{"derivedFrom":subQ4,"instanceName":"2"});var subQ7=makeQuery(id+"F15.boolean.opBoolean","COPY",FACE,{"disambiguationData":[TD([subQ0])],"derivedFrom":subQ3});var subQ8=makeQuery(id+"F16.opPattern","COPY",FACE,{"derivedFrom":subQ7,"instanceName":"2"});var subQ9=makeQuery(id+"F9.opRevolve","SWEPT_FACE",FACE,{"disambiguationData":[OSD([sQuery(id+"F8.wireOp",EDGE,"E21")])]});var subQ10=subQ9;var subQ11=makeQuery(id+"F18.opPattern","COPY",FACE,{"derivedFrom":subQ10,"instanceName":"1"});var subQ12=makeQuery(id+"F16.opPattern","COPY",FACE,{"derivedFrom":subQ10,"instanceName":"2"});var subQ13=makeQuery(id+"F16.opPattern","COPY",FACE,{"derivedFrom":subQ7,"instanceName":"1"});var subQ14=makeQuery(id+"F16.opPattern","COPY",FACE,{"derivedFrom":subQ4,"instanceName":"1"});var subQ15=makeQuery(id+"F16.opPattern","COPY",FACE,{"derivedFrom":subQ10,"instanceName":"1"});var subQ16=makeQuery(id+"F18.opPattern","COPY",FACE,{"derivedFrom":subQ10,"instanceName":"2"});var subQ17=sQuery(id+"F29.wireOp",EDGE,"E46");var subQ18=makeQuery(id+"F27.opExtrude","SWEPT_FACE",FACE,{"disambiguationData":[OSD([sQuery(id+"F26.wireOp",EDGE,"E38")])]});var subQ19=sQuery(id+"F29.wireOp",EDGE,"E47");Q1=makeQuery(id+"F34.boolean.opBoolean","SPLIT",EDGE,{"disambiguationData":[TD([makeQuery(id+"F30.opRevolve","SWEPT_FACE",FACE,{"disambiguationData":[OSD([subQ19])]})])],"derivedFrom":makeQuery(id+"F30.boolean.opBoolean","MERGE",EDGE,{"derivedFrom":[makeQuery(id+"F27.boolean.opBoolean","INTERSECT",EDGE,{"derivedFrom":[makeQuery(id+"F20.opBoolean","MERGE",FACE,{"derivedFrom":[subQ10,subQ7,subQ4,subQ15,subQ13,subQ14,subQ12,subQ8,subQ5,subQ11,subQ16]}),subQ18]}),makeQuery(id+"F30.opRevolve","CAP_EDGE",EDGE,{"disambiguationData":[OSD([subQ17])],"isStart":true})]})});}
            chamfer(context, id + "F40", {"entities" : qUnion([Q0, Q1]), "width" : 2.54 * mm, "tangentPropagation" : true});
        }
        {
            var Q0;
            {var subQ0=makeQuery(id+"F9.opRevolve","SWEPT_FACE",FACE,{"disambiguationData":[OSD([sQuery(id+"F8.wireOp",EDGE,"E21")])]});var subQ1=subQ0;var subQ2=makeQuery(id+"F16.opPattern","COPY",FACE,{"derivedFrom":subQ1,"instanceName":"2"});var subQ3=makeQuery(id+"F6.opRevolve","SWEPT_FACE",FACE,{"disambiguationData":[OSD([sQuery(id+"F5.wireOp",EDGE,"E16")])]});var subQ6=makeQuery(id+"F15.opRevolve","SWEPT_FACE",FACE,{"disambiguationData":[OSD([sQuery(id+"F14.wireOp",EDGE,"E26")])]});var subQ7=makeQuery(id+"F15.boolean.opBoolean","COPY",FACE,{"disambiguationData":[TD([subQ3])],"derivedFrom":subQ6});var subQ8=makeQuery(id+"F16.opPattern","COPY",FACE,{"derivedFrom":subQ7,"instanceName":"1"});var subQ9=makeQuery(id+"F15.boolean.opBoolean","COPY",FACE,{"disambiguationData":[TD([makeQuery(id+"F7.opPattern","COPY",FACE,{"derivedFrom":subQ3,"instanceName":"1"})])],"derivedFrom":subQ6});var subQ10=makeQuery(id+"F16.opPattern","COPY",FACE,{"derivedFrom":subQ9,"instanceName":"1"});var subQ11=makeQuery(id+"F16.opPattern","COPY",FACE,{"derivedFrom":subQ1,"instanceName":"1"});var subQ12=makeQuery(id+"F9.opRevolve","SWEPT_FACE",FACE,{"disambiguationData":[OSD([sQuery(id+"F8.wireOp",EDGE,"E20")])]});var subQ13=sQuery(id+"F31.wireOp",EDGE,"E49");var subQ14=makeQuery(id+"F16.opPattern","COPY",FACE,{"derivedFrom":subQ7,"instanceName":"2"});var subQ15=makeQuery(id+"F16.opPattern","COPY",FACE,{"derivedFrom":subQ9,"instanceName":"2"});var subQ16=makeQuery(id+"F18.opPattern","COPY",FACE,{"derivedFrom":subQ1,"instanceName":"1"});var subQ17=makeQuery(id+"F18.opPattern","COPY",FACE,{"derivedFrom":subQ1,"instanceName":"2"});var subQ18=makeQuery(id+"F27.opExtrude","SWEPT_FACE",FACE,{"disambiguationData":[OSD([sQuery(id+"F26.wireOp",EDGE,"E37")])]});Q0=makeQuery(id+"F35.boolean.opBoolean","SPLIT",EDGE,{"disambiguationData":[TD([subQ12])],"derivedFrom":makeQuery(id+"F32.boolean.opBoolean","MERGE",EDGE,{"derivedFrom":[makeQuery(id+"F27.boolean.opBoolean","INTERSECT",EDGE,{"derivedFrom":[makeQuery(id+"F20.opBoolean","MERGE",FACE,{"derivedFrom":[subQ1,subQ7,subQ9,subQ11,subQ8,subQ10,subQ2,subQ14,subQ15,subQ16,subQ17]}),subQ18]}),makeQuery(id+"F32.opRevolve","CAP_EDGE",EDGE,{"disambiguationData":[OSD([subQ13])],"isStart":true})]})});}
            var Q1;
            Q1=makeQuery(id+"F35.boolean.opBoolean","COPY",EDGE,{"derivedFrom":makeQuery(id+"F35.opExtrude","CAP_EDGE",EDGE,{"disambiguationData":[OSD([sQuery(id+"F28.wireOp",EDGE,"E44")])],"isStart":true})});
            var Q2;
            {var subQ0=makeQuery(id+"F6.opRevolve","SWEPT_FACE",FACE,{"disambiguationData":[OSD([sQuery(id+"F5.wireOp",EDGE,"E16")])]});var subQ3=makeQuery(id+"F15.opRevolve","SWEPT_FACE",FACE,{"disambiguationData":[OSD([sQuery(id+"F14.wireOp",EDGE,"E26")])]});var subQ4=makeQuery(id+"F15.boolean.opBoolean","COPY",FACE,{"disambiguationData":[TD([makeQuery(id+"F7.opPattern","COPY",FACE,{"derivedFrom":subQ0,"instanceName":"1"})])],"derivedFrom":subQ3});var subQ5=makeQuery(id+"F16.opPattern","COPY",FACE,{"derivedFrom":subQ4,"instanceName":"2"});var subQ6=makeQuery(id+"F15.boolean.opBoolean","COPY",FACE,{"disambiguationData":[TD([subQ0])],"derivedFrom":subQ3});var subQ7=makeQuery(id+"F16.opPattern","COPY",FACE,{"derivedFrom":subQ6,"instanceName":"2"});var subQ8=makeQuery(id+"F9.opRevolve","SWEPT_FACE",FACE,{"disambiguationData":[OSD([sQuery(id+"F8.wireOp",EDGE,"E21")])]});var subQ9=subQ8;var subQ10=makeQuery(id+"F18.opPattern","COPY",FACE,{"derivedFrom":subQ9,"instanceName":"1"});var subQ11=makeQuery(id+"F16.opPattern","COPY",FACE,{"derivedFrom":subQ9,"instanceName":"2"});var subQ12=makeQuery(id+"F16.opPattern","COPY",FACE,{"derivedFrom":subQ6,"instanceName":"1"});var subQ13=makeQuery(id+"F16.opPattern","COPY",FACE,{"derivedFrom":subQ4,"instanceName":"1"});var subQ14=makeQuery(id+"F16.opPattern","COPY",FACE,{"derivedFrom":subQ9,"instanceName":"1"});var subQ15=sQuery(id+"F31.wireOp",EDGE,"E49");var subQ16=makeQuery(id+"F18.opPattern","COPY",FACE,{"derivedFrom":subQ9,"instanceName":"2"});var subQ17=makeQuery(id+"F27.opExtrude","SWEPT_FACE",FACE,{"disambiguationData":[OSD([sQuery(id+"F26.wireOp",EDGE,"E37")])]});var subQ18=sQuery(id+"F31.wireOp",EDGE,"E48");Q2=makeQuery(id+"F35.boolean.opBoolean","SPLIT",EDGE,{"disambiguationData":[TD([makeQuery(id+"F32.opRevolve","SWEPT_FACE",FACE,{"disambiguationData":[OSD([subQ18])]})])],"derivedFrom":makeQuery(id+"F32.boolean.opBoolean","MERGE",EDGE,{"derivedFrom":[makeQuery(id+"F27.boolean.opBoolean","INTERSECT",EDGE,{"derivedFrom":[makeQuery(id+"F20.opBoolean","MERGE",FACE,{"derivedFrom":[subQ9,subQ6,subQ4,subQ14,subQ12,subQ13,subQ11,subQ7,subQ5,subQ10,subQ16]}),subQ17]}),makeQuery(id+"F32.opRevolve","CAP_EDGE",EDGE,{"disambiguationData":[OSD([subQ15])],"isStart":true})]})});}
            var Q3;
            Q3=makeQuery(id+"F35.boolean.opBoolean","COPY",EDGE,{"derivedFrom":makeQuery(id+"F35.opExtrude","CAP_EDGE",EDGE,{"disambiguationData":[OSD([sQuery(id+"F28.wireOp",EDGE,"E43")])],"isStart":true})});
            var Q4;
            Q4=makeQuery(id+"F35.boolean.opBoolean","COPY",EDGE,{"derivedFrom":makeQuery(id+"F35.opExtrude","CAP_EDGE",EDGE,{"disambiguationData":[OSD([sQuery(id+"F28.wireOp",EDGE,"E42")])],"isStart":true})});
            chamfer(context, id + "F41", {"entities" : qUnion([Q0, Q1, Q2, Q3, Q4]), "width" : 2.54 * mm, "tangentPropagation" : true});
        }
        {
            var Q0;
            {var subQ0=makeQuery(id+"F9.opRevolve","SWEPT_FACE",FACE,{"disambiguationData":[OSD([sQuery(id+"F8.wireOp",EDGE,"E22")])]});Q0=makeQuery(id+"F20.opBoolean","INTERSECT",EDGE,{"derivedFrom":[subQ0,makeQuery(id+"F16.opPattern","COPY",FACE,{"derivedFrom":makeQuery(id+"F7.opPattern","COPY",FACE,{"derivedFrom":makeQuery(id+"F6.opRevolve","SWEPT_FACE",FACE,{"disambiguationData":[OSD([sQuery(id+"F5.wireOp",EDGE,"E16")])]}),"instanceName":"1"}),"instanceName":"1"}),makeQuery(id+"F16.opPattern","COPY",FACE,{"derivedFrom":subQ0,"instanceName":"2"}),makeQuery(id+"F18.opPattern","COPY",FACE,{"derivedFrom":subQ0,"instanceName":"1"}),makeQuery(id+"F18.opPattern","COPY",FACE,{"derivedFrom":subQ0,"instanceName":"2"}),makeQuery(id+"F16.opPattern","COPY",FACE,{"derivedFrom":subQ0,"instanceName":"1"})]});}
            fillet(context, id + "F42", {"entities" : qUnion([Q0]), "radius" : 5.08 * mm, "tangentPropagation" : true, "allowEdgeOverflow" : false});
        }
        {
            var Q0;
            {var subQ0=makeQuery(id+"F9.opRevolve","SWEPT_FACE",FACE,{"disambiguationData":[OSD([sQuery(id+"F8.wireOp",EDGE,"E22")])]});Q0=makeQuery(id+"F20.opBoolean","INTERSECT",EDGE,{"derivedFrom":[makeQuery(id+"F16.opPattern","COPY",FACE,{"derivedFrom":subQ0,"instanceName":"2"}),makeQuery(id+"F16.opPattern","COPY",FACE,{"derivedFrom":makeQuery(id+"F6.opRevolve","SWEPT_FACE",FACE,{"disambiguationData":[OSD([sQuery(id+"F5.wireOp",EDGE,"E16")])]}),"instanceName":"2"}),makeQuery(id+"F18.opPattern","COPY",FACE,{"derivedFrom":subQ0,"instanceName":"2"})]});}
            fillet(context, id + "F43", {"entities" : qUnion([Q0]), "radius" : 5.08 * mm, "tangentPropagation" : true, "allowEdgeOverflow" : false});
        }
        {
            var Q0;
            Q0=makeQuery(id+"F25.boolean.opBoolean","COPY",FACE,{"derivedFrom":makeQuery(id+"F25.opPattern","COPY",FACE,{"derivedFrom":makeQuery(id+"F24.opExtrude","SWEPT_FACE",FACE,{"disambiguationData":[OSD([sQuery(id+"F23.wireOp",EDGE,"E36")])]}),"instanceName":"2"})});
            var Q1;
            Q1=makeQuery(id+"F25.boolean.opBoolean","COPY",FACE,{"derivedFrom":makeQuery(id+"F25.opPattern","COPY",FACE,{"derivedFrom":makeQuery(id+"F24.opExtrude","CAP_FACE",FACE,{"disambiguationData":[OSD([sQuery(id+"F23.wireOp",EDGE,"E36")])],"isStart":true}),"instanceName":"2"})});
            fillet(context, id + "F44", {"entities" : qUnion([Q0, Q1]), "radius" : 2.03 * mm, "tangentPropagation" : true, "allowEdgeOverflow" : false});
        }
    });
